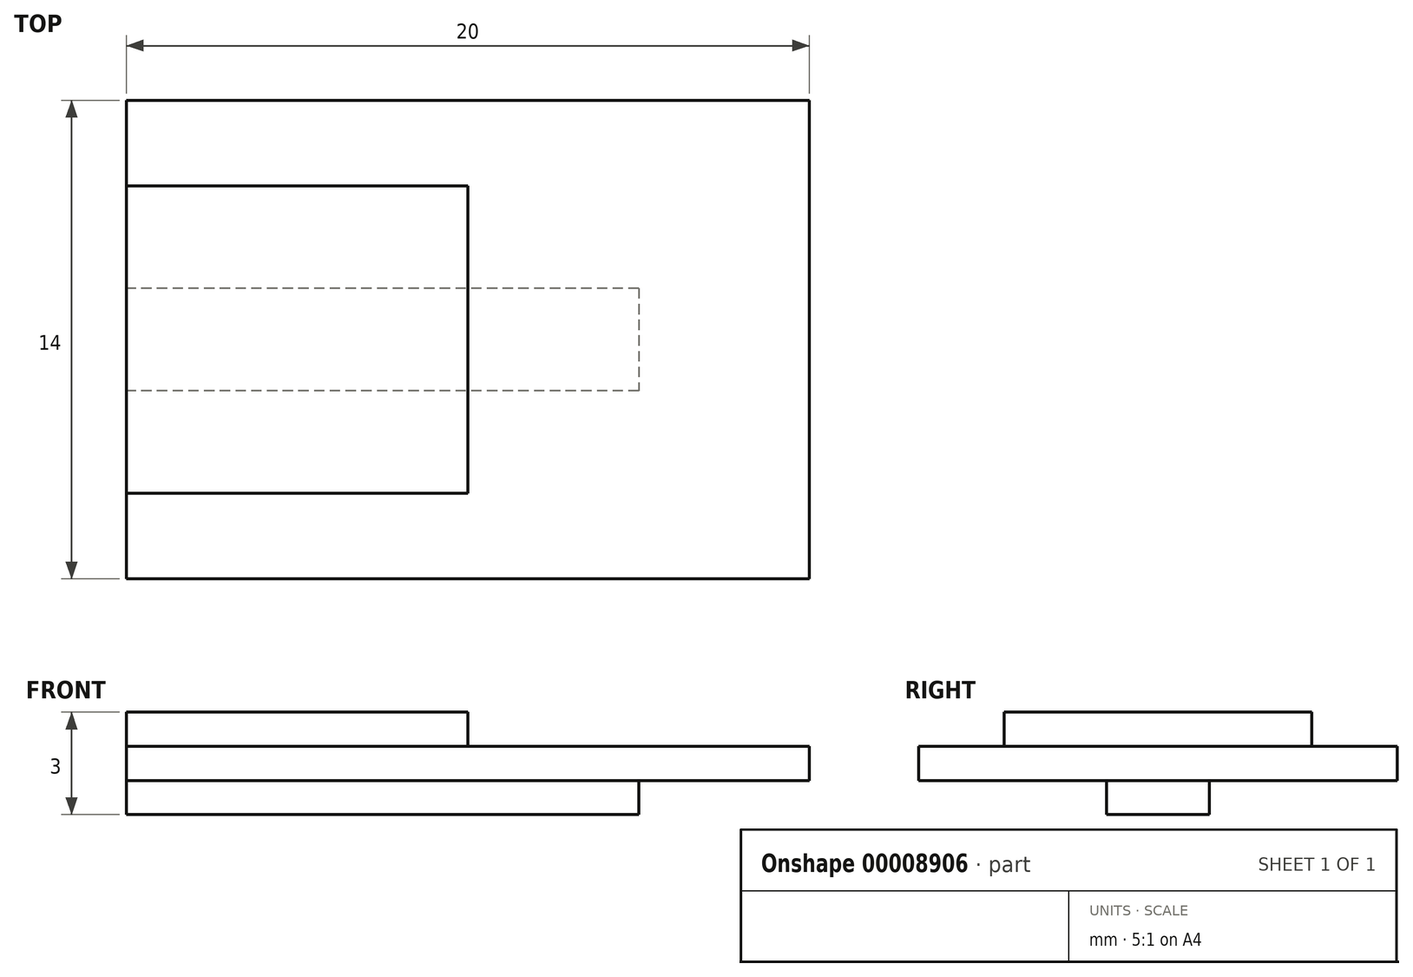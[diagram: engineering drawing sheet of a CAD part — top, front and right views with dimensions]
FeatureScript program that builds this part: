
annotation { "Feature Type Name" : "Feature", "Feature Type Description" : "" }
export const myFeature = defineFeature(function(context is Context, id is Id, definition is map)
    precondition{}
    {
        {
            var Q0;
            Q0=qCreatedBy(makeId("Top.planeOp"),FACE);
            var sketch = newSketch(context, id + "F0", { "sketchPlane" : qUnion([Q0])});
            skLineSegment(sketch, "E0", {"start": v(0, 0) * mm, "end": v(-10, 0) * mm});
            skLineSegment(sketch, "E1", {"start": v(0, 0) * mm, "end": v(10, 0) * mm});
            skLineSegment(sketch, "E2.0", {"start": v(0, 7.5) * mm, "end": v(-10, 7.5) * mm});
            skLineSegment(sketch, "E3.0", {"start": v(0, -7.5) * mm, "end": v(-10, -7.5) * mm});
            skLineSegment(sketch, "E4.0", {"start": v(0, -7.5) * mm, "end": v(10, -7.5) * mm});
            skLineSegment(sketch, "E5.0", {"start": v(0, 7.5) * mm, "end": v(10, 7.5) * mm});
            skLineSegment(sketch, "E6", {"start": v(-10, 0) * mm, "end": v(-10, -7.5) * mm});
            skLineSegment(sketch, "E7", {"start": v(-10, 0) * mm, "end": v(-10, 7.5) * mm});
            skLineSegment(sketch, "E8", {"start": v(10, 0) * mm, "end": v(10, 7.5) * mm});
            skLineSegment(sketch, "E9", {"start": v(10, 0) * mm, "end": v(10, -7.5) * mm});
            skSolve(sketch);
        }
        {
            var Q0;
            Q0=makeQuery(id+"F0.imprint","IMPRINT",FACE,{"disambiguationData":[TD([[makeQuery(id+"F0.imprint","IMPRINT",EDGE,{"derivedFrom":sQuery(id+"F0.wireOp",EDGE,"E0")}),-1.0]])]});
            var Q1;
            Q1=makeQuery(id+"F0.imprint","IMPRINT",FACE,{"disambiguationData":[TD([[makeQuery(id+"F0.imprint","IMPRINT",EDGE,{"derivedFrom":sQuery(id+"F0.wireOp",EDGE,"E0")}),1.0]])]});
            extrude(context, id + "F1", {"entities" : qUnion([Q0, Q1]), "depth" : 4 * mm});
        }
        {
            var Q0;
            Q0=makeQuery(id+"F1.opExtrude","SWEPT_FACE",FACE,{"disambiguationData":[OSD([sQuery(id+"F0.wireOp",EDGE,"E8"),sQuery(id+"F0.wireOp",EDGE,"E9")])]});
            var sketch = newSketch(context, id + "F2", { "sketchPlane" : qUnion([Q0])});
            skLineSegment(sketch, "E10", {"start": v(0, 0) * mm, "end": v(0, 1) * mm});
            skLineSegment(sketch, "E11.0", {"start": v(2, 0) * mm, "end": v(2, 1) * mm});
            skLineSegment(sketch, "E12.0", {"start": v(-2, 0) * mm, "end": v(-2, 1) * mm});
            skLineSegment(sketch, "E13", {"start": v(0, 1) * mm, "end": v(-7.5, 1) * mm});
            skLineSegment(sketch, "E14", {"start": v(0, 1) * mm, "end": v(7.5, 1) * mm});
            skLineSegment(sketch, "E15.0", {"start": v(0, 3) * mm, "end": v(-8.23, 3) * mm});
            skLineSegment(sketch, "E15.1", {"start": v(0, 3) * mm, "end": v(7.5, 3) * mm});
            skLineSegment(sketch, "E16", {"start": v(0, 3) * mm, "end": v(0, 4) * mm});
            skLineSegment(sketch, "E17.0", {"start": v(5, 3) * mm, "end": v(5, 4) * mm});
            skLineSegment(sketch, "E18.0", {"start": v(-5, 3) * mm, "end": v(-5, 4) * mm});
            skLineSegment(sketch, "E19", {"start": v(-7.5, 1) * mm, "end": v(-7.5, 3) * mm});
            skLineSegment(sketch, "E20", {"start": v(7.5, 1) * mm, "end": v(7.5, 3.07) * mm});
            skSolve(sketch);
        }
        {
            var Q0;
            {var subQ2=sQuery(id+"F2.wireOp",EDGE,"E12.0");Q0=makeQuery(id+"F2.imprint","IMPRINT",FACE,{"disambiguationData":[TD([[makeQuery(id+"F2.imprint","IMPRINT",EDGE,{"derivedFrom":subQ2}),1.0]])]});}
            var Q1;
            {var subQ2=sQuery(id+"F2.wireOp",EDGE,"E11.0");Q1=makeQuery(id+"F2.imprint","IMPRINT",FACE,{"disambiguationData":[TD([[makeQuery(id+"F2.imprint","IMPRINT",EDGE,{"derivedFrom":subQ2}),-1.0]])]});}
            var Q2;
            {var subQ2=sQuery(id+"F2.wireOp",EDGE,"E18.0");Q2=makeQuery(id+"F2.imprint","IMPRINT",FACE,{"disambiguationData":[TD([[makeQuery(id+"F2.imprint","IMPRINT",EDGE,{"derivedFrom":subQ2}),1.0]])]});}
            var Q3;
            {var subQ2=sQuery(id+"F2.wireOp",EDGE,"E17.0");Q3=makeQuery(id+"F2.imprint","IMPRINT",FACE,{"disambiguationData":[TD([[makeQuery(id+"F2.imprint","IMPRINT",EDGE,{"derivedFrom":subQ2}),-1.0]])]});}
            extrude(context, id + "F3", {"entities" : qUnion([Q0, Q1, Q2, Q3]), "operationType" : NewBodyOperationType.REMOVE, "oppositeDirection" : true, "depth" : 25 * mm});
        }
        {
            var Q0;
            Q0=makeQuery(id+"F1.opExtrude","SWEPT_FACE",FACE,{"disambiguationData":[OSD([sQuery(id+"F0.wireOp",EDGE,"E8"),sQuery(id+"F0.wireOp",EDGE,"E9")])]});
            var sketch = newSketch(context, id + "F4", { "sketchPlane" : qUnion([Q0])});
            skLineSegment(sketch, "E21", {"start": v(5, 3) * mm, "end": v(-5, 3) * mm});
            skLineSegment(sketch, "E22", {"start": v(2, 1) * mm, "end": v(-2, 1) * mm});
            skSolve(sketch);
        }
        {
            var Q0;
            Q0=makeQuery(id+"F4.imprint","IMPRINT",FACE,{"disambiguationData":[TD([[makeQuery(id+"F4.imprint","IMPRINT",EDGE,{"derivedFrom":sQuery(id+"F4.wireOp",EDGE,"E21")}),-1.0]])]});
            var Q1;
            Q1=makeQuery(id+"F4.imprint","IMPRINT",FACE,{"disambiguationData":[TD([[makeQuery(id+"F4.imprint","IMPRINT",EDGE,{"derivedFrom":sQuery(id+"F4.wireOp",EDGE,"E22")}),1.0]])]});
            extrude(context, id + "F5", {"entities" : qUnion([Q0, Q1]), "operationType" : NewBodyOperationType.REMOVE, "oppositeDirection" : true, "depth" : 5 * mm});
        }
        {
            var Q0;
            Q0=makeQuery(id+"F5.boolean.opBoolean","COPY",FACE,{"derivedFrom":makeQuery(id+"F5.opExtrude","CAP_FACE",FACE,{"disambiguationData":[OSD([sQuery(id+"F0.wireOp",EDGE,"E8"),sQuery(id+"F0.wireOp",EDGE,"E9"),sQuery(id+"F2.wireOp",EDGE,"E17.0"),sQuery(id+"F2.wireOp",EDGE,"E18.0"),sQuery(id+"F4.wireOp",EDGE,"E21")])],"isStart":false})});
            extrude(context, id + "F6", {"entities" : qUnion([Q0]), "operationType" : NewBodyOperationType.REMOVE, "oppositeDirection" : true, "depth" : 5 * mm});
        }
        {
            var Q0;
            Q0=makeQuery(id+"F1.opExtrude","SWEPT_FACE",FACE,{"disambiguationData":[OSD([sQuery(id+"F0.wireOp",EDGE,"E6"),sQuery(id+"F0.wireOp",EDGE,"E7")])]});
            var sketch = newSketch(context, id + "F7", { "sketchPlane" : qUnion([Q0])});
            skLineSegment(sketch, "E23.0", {"start": v(4.5, 3.5) * mm, "end": v(4.5, 2.5) * mm});
            skLineSegment(sketch, "E23.1", {"start": v(7, 2.5) * mm, "end": v(4.5, 2.5) * mm});
            skLineSegment(sketch, "E23.2", {"start": v(7, 2.5) * mm, "end": v(7, 1.5) * mm});
            skLineSegment(sketch, "E23.3", {"start": v(7, 1.5) * mm, "end": v(1.5, 1.5) * mm});
            skLineSegment(sketch, "E23.4", {"start": v(1.5, 1.5) * mm, "end": v(1.5, 0.5) * mm});
            skLineSegment(sketch, "E23.5", {"start": v(4.5, 3.5) * mm, "end": v(-4.5, 3.5) * mm});
            skLineSegment(sketch, "E23.6", {"start": v(1.5, 0.5) * mm, "end": v(-1.5, 0.5) * mm});
            skLineSegment(sketch, "E23.7", {"start": v(-1.5, 1.5) * mm, "end": v(-1.5, 0.5) * mm});
            skLineSegment(sketch, "E23.8", {"start": v(-7, 1.5) * mm, "end": v(-1.5, 1.5) * mm});
            skLineSegment(sketch, "E23.9", {"start": v(-7, 2.5) * mm, "end": v(-7, 1.5) * mm});
            skLineSegment(sketch, "E23.10", {"start": v(-7, 2.5) * mm, "end": v(-4.5, 2.5) * mm});
            skLineSegment(sketch, "E23.11", {"start": v(-4.5, 3.5) * mm, "end": v(-4.5, 2.5) * mm});
            skSolve(sketch);
        }
        {
            var Q0;
            Q0=makeQuery(id+"F7.imprint","IMPRINT",FACE,{"disambiguationData":[TD([[makeQuery(id+"F7.imprint","IMPRINT",EDGE,{"derivedFrom":sQuery(id+"F7.wireOp",EDGE,"E23.0")}),1.0]])]});
            extrude(context, id + "F8", {"entities" : qUnion([Q0]), "operationType" : NewBodyOperationType.REMOVE, "oppositeDirection" : true, "depth" : 25 * mm});
        }
        {
            var Q0;
            Q0=makeQuery(id+"F1.opExtrude","SWEPT_FACE",FACE,{"disambiguationData":[OSD([sQuery(id+"F0.wireOp",EDGE,"E8"),sQuery(id+"F0.wireOp",EDGE,"E9")])]});
            var sketch = newSketch(context, id + "F9", { "sketchPlane" : qUnion([Q0])});
            skLineSegment(sketch, "E24.0", {"start": v(4.5, 2.5) * mm, "end": v(-4.5, 2.5) * mm});
            skSolve(sketch);
        }
        {
            var Q0;
            Q0=makeQuery(id+"F9.imprint","IMPRINT",FACE,{"disambiguationData":[TD([[makeQuery(id+"F9.imprint","IMPRINT",EDGE,{"derivedFrom":sQuery(id+"F9.wireOp",EDGE,"E24.0")}),-1.0]])]});
            extrude(context, id + "F10", {"entities" : qUnion([Q0]), "operationType" : NewBodyOperationType.REMOVE, "oppositeDirection" : true, "depth" : 10 * mm});
        }
        {
            var Q0;
            Q0=makeQuery(id+"F1.opExtrude","SWEPT_FACE",FACE,{"disambiguationData":[OSD([sQuery(id+"F0.wireOp",EDGE,"E8"),sQuery(id+"F0.wireOp",EDGE,"E9")])]});
            var sketch = newSketch(context, id + "F11", { "sketchPlane" : qUnion([Q0])});
            skLineSegment(sketch, "E25.0", {"start": v(-1.5, 1.5) * mm, "end": v(1.5, 1.5) * mm});
            skSolve(sketch);
        }
        {
            var Q0;
            Q0=makeQuery(id+"F11.imprint","IMPRINT",FACE,{"disambiguationData":[TD([[makeQuery(id+"F11.imprint","IMPRINT",EDGE,{"derivedFrom":sQuery(id+"F11.wireOp",EDGE,"E25.0")}),-1.0]])]});
            extrude(context, id + "F12", {"entities" : qUnion([Q0]), "operationType" : NewBodyOperationType.REMOVE, "oppositeDirection" : true, "depth" : 5 * mm});
        }
    });
